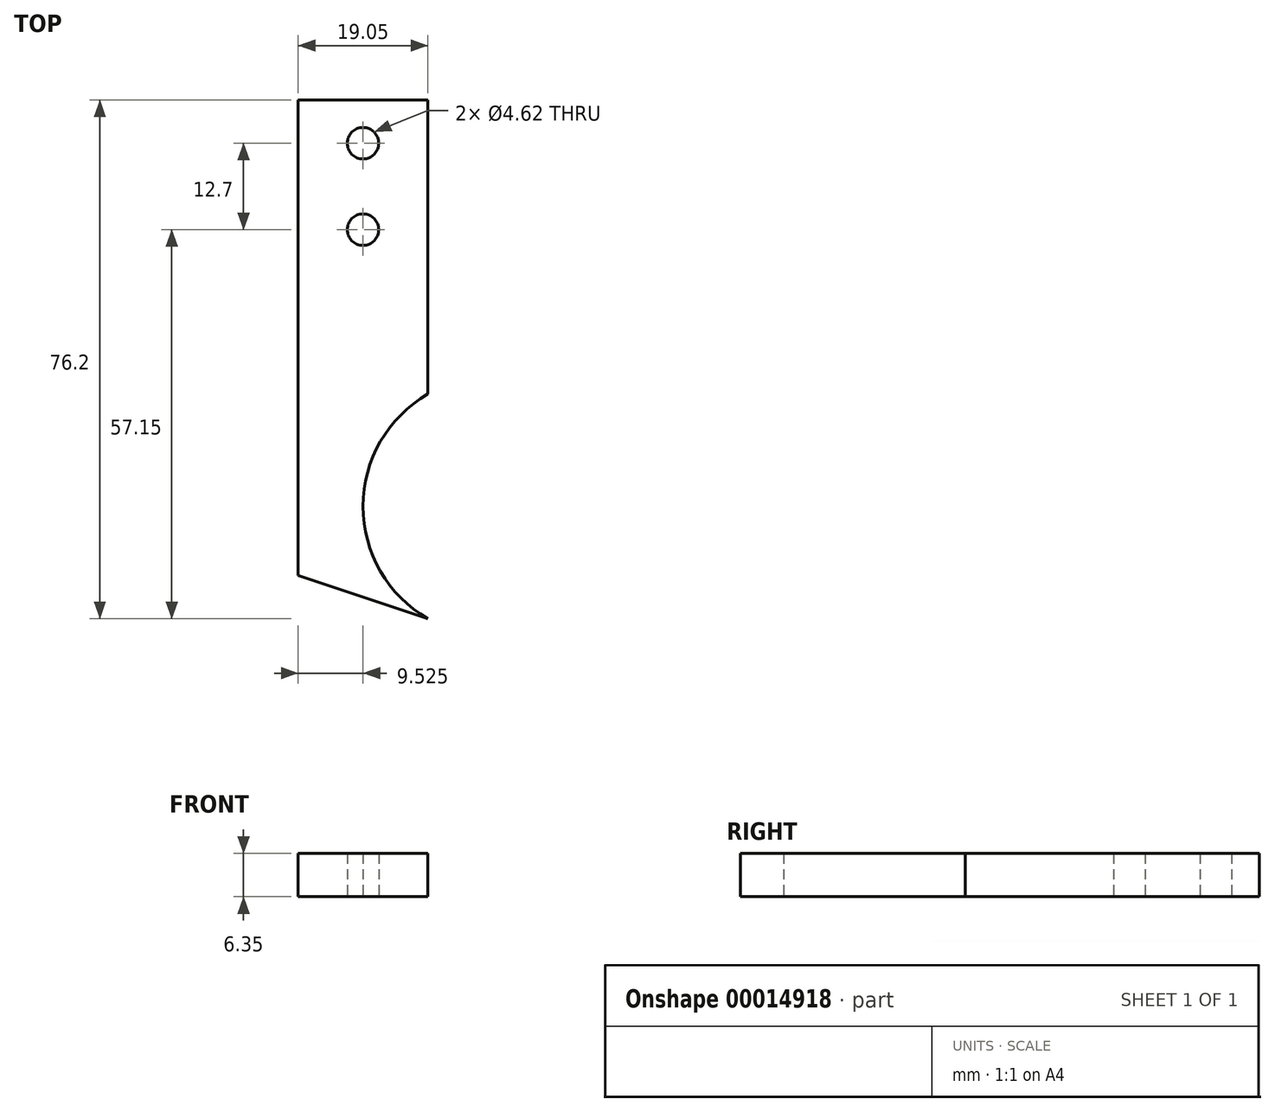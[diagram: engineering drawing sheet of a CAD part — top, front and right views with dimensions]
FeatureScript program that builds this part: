
annotation { "Feature Type Name" : "Feature", "Feature Type Description" : "" }
export const myFeature = defineFeature(function(context is Context, id is Id, definition is map)
    precondition{}
    {
        {
            var Q0;
            Q0=qCreatedBy(makeId("Top.planeOp"),FACE);
            var sketch = newSketch(context, id + "F0", { "sketchPlane" : qUnion([Q0])});
            skLineSegment(sketch, "E0.bottom", {"start": v(0, 76.2) * mm, "end": v(19.05, 76.2) * mm});
            skLineSegment(sketch, "E0.top", {"start": v(0, 0) * mm, "end": v(19.05, 0) * mm});
            skLineSegment(sketch, "E0.left", {"start": v(0, 76.2) * mm, "end": v(0, 0) * mm});
            skLineSegment(sketch, "E0.right", {"start": v(19.05, 76.2) * mm, "end": v(19.05, 0) * mm});
            skCircle(sketch, "E1", {"center": v(28.58, 16.5) * mm, "radius": 19.05 * mm});
            skCircle(sketch, "E2", {"center": v(9.52, 69.85) * mm, "radius": 2.31 * mm});
            skLineSegment(sketch, "E3", {"start": v(19.05, 0) * mm, "end": v(0, 6.35) * mm});
            skCircle(sketch, "E4", {"center": v(9.53, 57.15) * mm, "radius": 2.31 * mm});
            skSolve(sketch);
        }
        {
            var Q0;
            {var subQ4=sQuery(id+"F0.wireOp",EDGE,"E0.bottom");Q0=makeQuery(id+"F0.imprint","IMPRINT",FACE,{"disambiguationData":[TD([[makeQuery(id+"F0.imprint","IMPRINT",EDGE,{"derivedFrom":subQ4}),-1.0]])]});}
            extrude(context, id + "F1", {"entities" : qUnion([Q0]), "depth" : 6.35 * mm});
        }
    });
